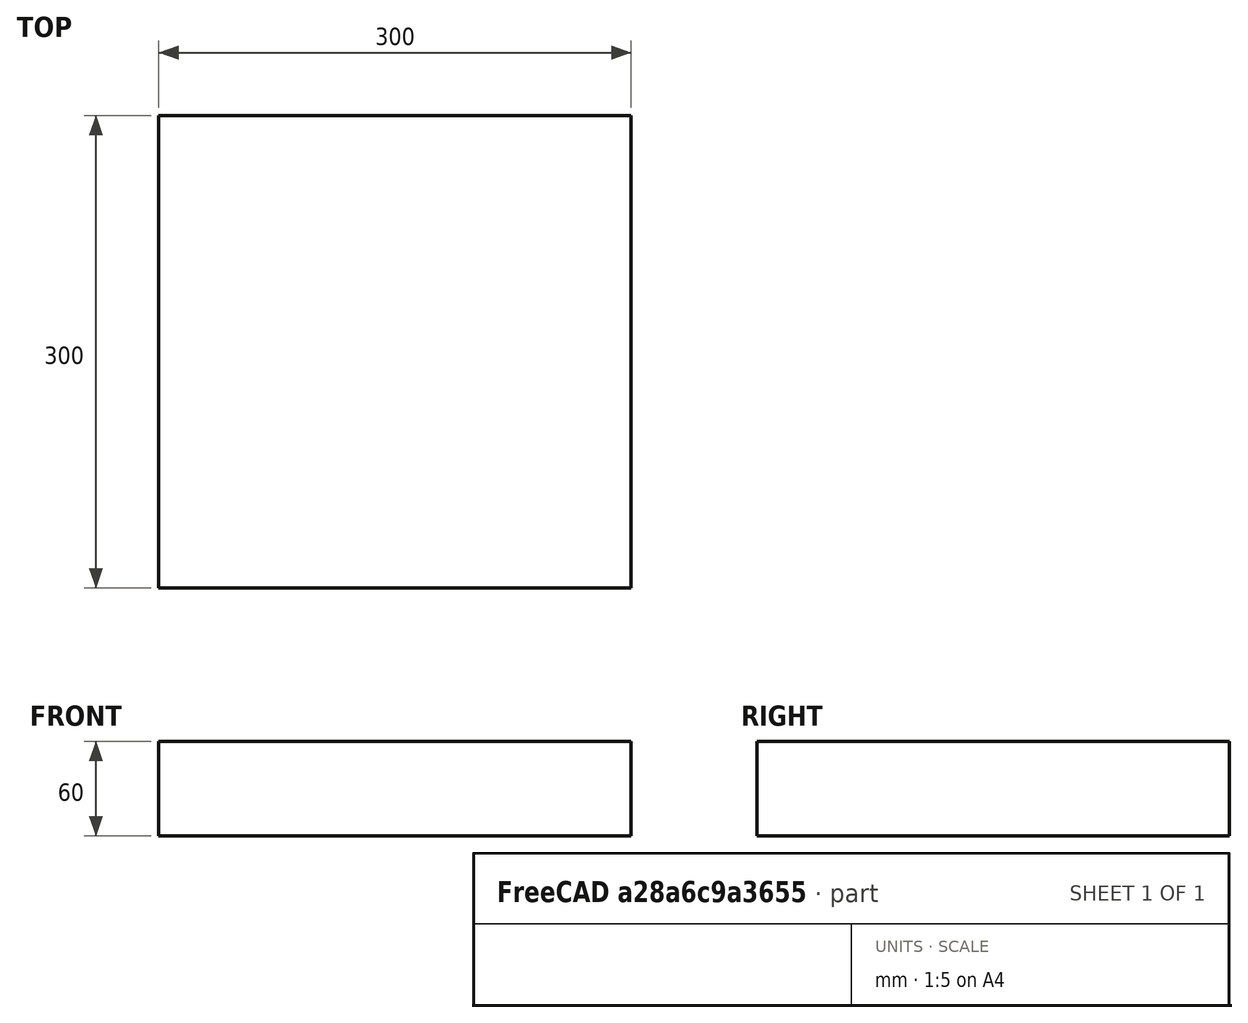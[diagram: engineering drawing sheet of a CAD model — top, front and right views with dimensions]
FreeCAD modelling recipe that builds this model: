
FCSTD DOCUMENT  (FreeCAD 0.18R16131 (Git))
Label: Iinnexxyy_top_test
License: All rights reserved
LicenseURL: http://en.wikipedia.org/wiki/All_rights_reserved
objects: Sketcher::SketchObject×2, Part::Extrusion×1
note: 3 computed .brp shape members not serialized (recipe doc carries the construction recipe); baked Part::Feature solids carry a one-line shape summary decoded from their .brp

FEATURE [Sketcher::SketchObject] Sketch
  sketch-geometry (4):
    g0: LineSegment StartX=-121.808 StartY=-106.368 StartZ=0 EndX=178.192 EndY=-106.368 EndZ=0
    g1: LineSegment StartX=178.192 StartY=-106.368 StartZ=0 EndX=178.192 EndY=193.632 EndZ=0
    g2: LineSegment StartX=178.192 StartY=193.632 StartZ=0 EndX=-121.808 EndY=193.632 EndZ=0
    g3: LineSegment StartX=-121.808 StartY=193.632 StartZ=0 EndX=-121.808 EndY=-106.368 EndZ=0
  constraints (6):
    c: Horizontal(g0)
    c: Horizontal(g2)
    c: Vertical(g1)
    c: Vertical(g3)
    c: DistanceY(g3,g3) = 300
    c: DistanceX(g2,g2) = 300
FEATURE [Part::Extrusion] Extrude
  Base = -> Sketch
  Dir = (0,0,1)
  DirMode = 2
  FaceMakerClass = Part::FaceMakerBullseye
  LengthFwd = 60
  LengthRev = 0
  Solid = true
  Symmetric = false
FEATURE [Sketcher::SketchObject] Sketch001
  ExternalGeometry = -> [Extrude]
  MapMode = 5
  Placement = pos=(0,0,60) rot=(0,0,1;0rad)
  Support = -> [Extrude]
  sketch-geometry (16):
    g0: LineSegment StartX=-121.808 StartY=53.6317 StartZ=0 EndX=18.1921 EndY=53.6317 EndZ=0
    g1: LineSegment StartX=18.1921 StartY=53.6317 StartZ=0 EndX=18.1921 EndY=193.632 EndZ=0
    g2: LineSegment StartX=18.1921 StartY=193.632 StartZ=0 EndX=-121.808 EndY=193.632 EndZ=0
    g3: LineSegment StartX=-121.808 StartY=193.632 StartZ=0 EndX=-121.808 EndY=53.6317 EndZ=0
    g4: LineSegment StartX=38.2404 StartY=53.6317 StartZ=0 EndX=178.24 EndY=53.6317 EndZ=0
    g5: LineSegment StartX=178.24 StartY=53.6317 StartZ=0 EndX=178.24 EndY=193.632 EndZ=0
    g6: LineSegment StartX=178.24 StartY=193.632 StartZ=0 EndX=38.2404 EndY=193.632 EndZ=0
    g7: LineSegment StartX=38.2404 StartY=193.632 StartZ=0 EndX=38.2404 EndY=53.6317 EndZ=0
    g8: LineSegment StartX=-121.808 StartY=33.6317 StartZ=0 EndX=18.1921 EndY=33.6317 EndZ=0
    g9: LineSegment StartX=18.1921 StartY=33.6317 StartZ=0 EndX=18.1921 EndY=-106.368 EndZ=0
    g10: LineSegment StartX=18.1921 StartY=-106.368 StartZ=0 EndX=-121.808 EndY=-106.368 EndZ=0
    g11: LineSegment StartX=-121.808 StartY=-106.368 StartZ=0 EndX=-121.808 EndY=33.6317 EndZ=0
    g12: LineSegment StartX=38.5808 StartY=33.6317 StartZ=0 EndX=178.581 EndY=33.6317 EndZ=0
    g13: LineSegment StartX=178.581 StartY=33.6317 StartZ=0 EndX=178.581 EndY=-106.368 EndZ=0
    g14: LineSegment StartX=178.581 StartY=-106.368 StartZ=0 EndX=38.5808 EndY=-106.368 EndZ=0
    g15: LineSegment StartX=38.5808 StartY=-106.368 StartZ=0 EndX=38.5808 EndY=33.6317 EndZ=0
  constraints (46):
    c: Coincident(g0,g1)
    c: Coincident(g1,g2)
    c: Coincident(g2,g3)
    c: Coincident(g3,g0)
    c: Horizontal(g0)
    c: Horizontal(g2)
    c: Vertical(g1)
    c: Vertical(g3)
    c: DistanceX(g2,g2) = 140
    c: DistanceY(g1,g1) = 140
    c: Coincident(g4,g5)
    c: Coincident(g5,g6)
    c: Coincident(g6,g7)
    c: Coincident(g7,g4)
    c: Horizontal(g4)
    c: Horizontal(g6)
    c: Vertical(g5)
    c: Vertical(g7)
    c: DistanceX(g6,g6) = 140
    c: DistanceY(g5,g5) = 140
    c: Coincident(g8,g9)
    c: Coincident(g9,g10)
    c: Coincident(g10,g11)
    c: Coincident(g11,g8)
    c: Horizontal(g8)
    c: Horizontal(g10)
    c: Vertical(g9)
    c: Vertical(g11)
    c: DistanceX(g8,g8) = 140
    c: DistanceY(g9,g9) = 140
    c: Coincident(g12,g13)
    c: Coincident(g13,g14)
    c: Coincident(g14,g15)
    c: Coincident(g15,g12)
    c: Horizontal(g12)
    c: Horizontal(g14)
    c: Vertical(g13)
    c: Vertical(g15)
    c: DistanceX(g12,g12) = 140
    c: DistanceY(g15,g15) = 140
    c: DistanceX(g-3,g2) = 0
    c: DistanceY(g2,g-3) = 0
    c: DistanceY(g5,g-3) = 0
    c: DistanceY(g-4,g13) = 0
    c: DistanceY(g10,g-4) = 0
    c: DistanceX(g-4,g10) = 0
